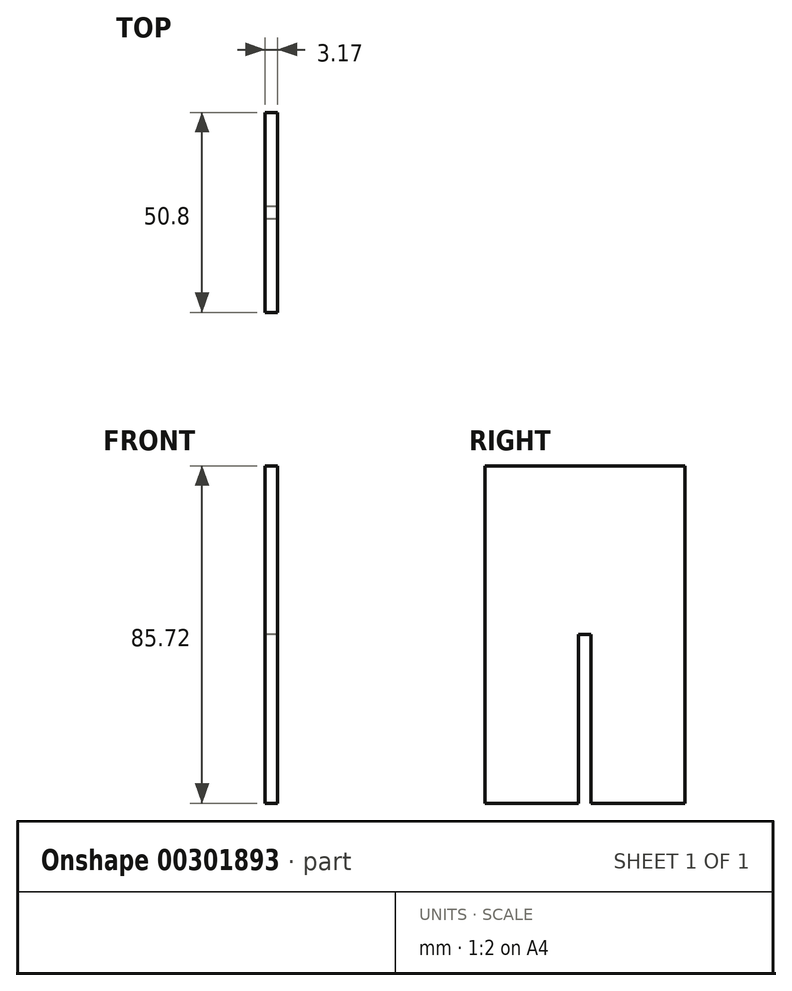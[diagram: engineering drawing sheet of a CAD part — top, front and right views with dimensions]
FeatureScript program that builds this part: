
annotation { "Feature Type Name" : "Feature", "Feature Type Description" : "" }
export const myFeature = defineFeature(function(context is Context, id is Id, definition is map)
    precondition{}
    {
        {
            var Q0;
            Q0=qCreatedBy(makeId("Right.planeOp"),FACE);
            var sketch = newSketch(context, id + "F0", { "sketchPlane" : qUnion([Q0])});
            skLineSegment(sketch, "E0.bottom", {"start": v(-25.4, -42.86) * mm, "end": v(25.4, -42.86) * mm});
            skLineSegment(sketch, "E0.top", {"start": v(-25.4, 42.86) * mm, "end": v(25.4, 42.86) * mm});
            skLineSegment(sketch, "E0.left", {"start": v(-25.4, -42.86) * mm, "end": v(-25.4, 42.86) * mm});
            skLineSegment(sketch, "E0.right", {"start": v(25.4, -42.86) * mm, "end": v(25.4, 42.86) * mm});
            skPoint(sketch, "E0.middle", {"position": v(0, 0) * mm});
            skLineSegment(sketch, "E1.bottom", {"start": v(-1.72, -42.86) * mm, "end": v(1.46, -42.86) * mm});
            skLineSegment(sketch, "E1.top", {"start": v(-1.72, 0) * mm, "end": v(1.46, 0) * mm});
            skLineSegment(sketch, "E1.left", {"start": v(-1.72, -42.86) * mm, "end": v(-1.72, 0) * mm});
            skLineSegment(sketch, "E1.right", {"start": v(1.46, -42.86) * mm, "end": v(1.46, 0) * mm});
            skSolve(sketch);
        }
        {
            var Q0;
            Q0=makeQuery(id+"F0.imprint","IMPRINT",FACE,{"disambiguationData":[TD([[makeQuery(id+"F0.imprint","IMPRINT",EDGE,{"derivedFrom":sQuery(id+"F0.wireOp",EDGE,"E0.bottom")}),1.0]])]});
            extrude(context, id + "F1", {"entities" : qUnion([Q0]), "depth" : 3.17 * mm});
        }
    });
